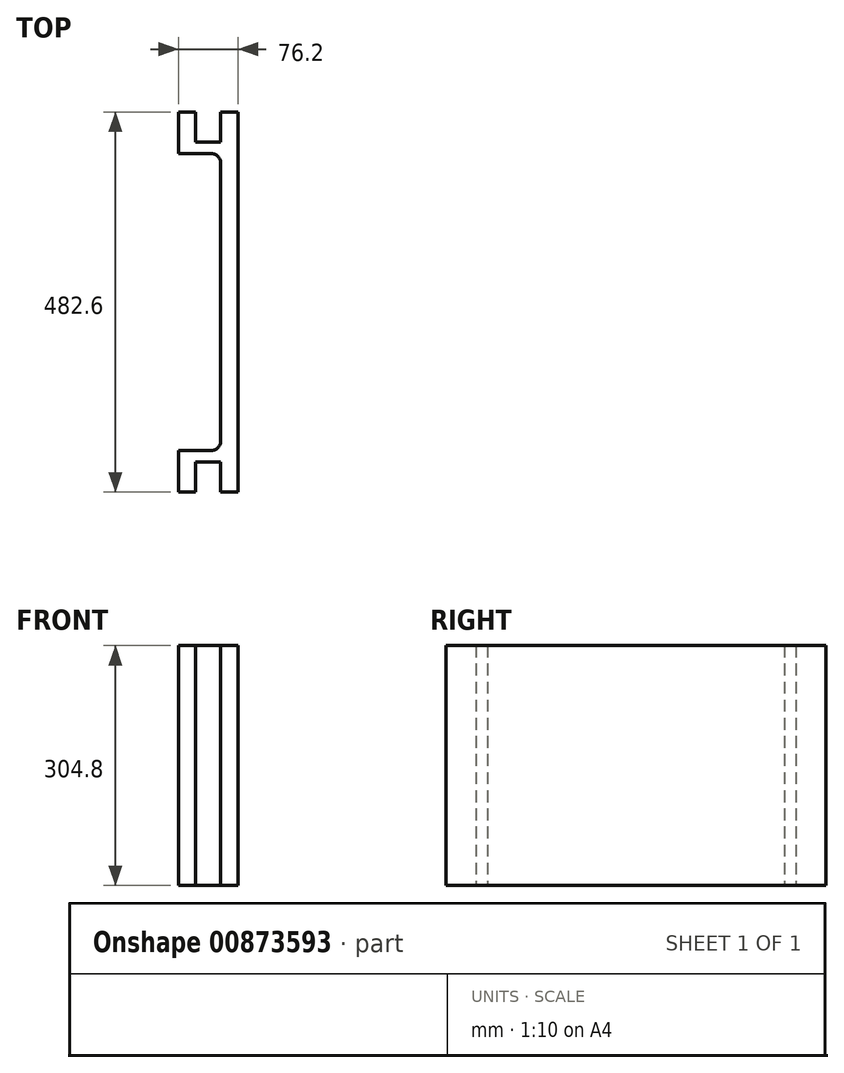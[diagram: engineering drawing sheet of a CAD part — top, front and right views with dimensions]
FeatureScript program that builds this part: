
annotation { "Feature Type Name" : "Feature", "Feature Type Description" : "" }
export const myFeature = defineFeature(function(context is Context, id is Id, definition is map)
    precondition{}
    {
        {
            var Q0;
            Q0=qCreatedBy(makeId("Top.planeOp"),FACE);
            var sketch = newSketch(context, id + "F0", { "sketchPlane" : qUnion([Q0])});
            skLineSegment(sketch, "E0.bottom", {"start": v(0, 0) * mm, "end": v(22.22, 0) * mm});
            skLineSegment(sketch, "E0.top", {"start": v(0, 482.6) * mm, "end": v(22.22, 482.6) * mm});
            skLineSegment(sketch, "E0.right", {"start": v(76.2, 0) * mm, "end": v(76.2, 482.6) * mm});
            skLineSegment(sketch, "E1", {"start": v(0, 241.3) * mm, "end": v(242.2, 241.3) * mm, "construction": true});
            skLineSegment(sketch, "E2", {"start": v(38.1, 482.6) * mm, "end": v(38.1, -58.83) * mm, "construction": true});
            skLineSegment(sketch, "E3", {"start": v(22.22, 482.6) * mm, "end": v(22.22, 444.5) * mm});
            skLineSegment(sketch, "E4", {"start": v(22.22, 444.5) * mm, "end": v(53.98, 444.5) * mm});
            skLineSegment(sketch, "E5", {"start": v(53.97, 444.5) * mm, "end": v(53.97, 482.6) * mm});
            skLineSegment(sketch, "E6.trimOffspring", {"start": v(53.98, 482.6) * mm, "end": v(76.2, 482.6) * mm});
            skLineSegment(sketch, "E7.MirrorCS", {"start": v(22.22, 0) * mm, "end": v(22.22, 38.1) * mm});
            skLineSegment(sketch, "E8.MirrorCS", {"start": v(22.22, 38.1) * mm, "end": v(53.97, 38.1) * mm});
            skLineSegment(sketch, "E9.MirrorCS", {"start": v(53.97, 38.1) * mm, "end": v(53.97, 0) * mm});
            skLineSegment(sketch, "E10.trimOffspring", {"start": v(53.97, 0) * mm, "end": v(76.2, 0) * mm});
            skLineSegment(sketch, "E11.bottom", {"start": v(53.97, 430.05) * mm, "end": v(22.22, 430.05) * mm});
            skLineSegment(sketch, "E11.top", {"start": v(53.98, 52.55) * mm, "end": v(22.22, 52.55) * mm});
            skLineSegment(sketch, "E11.left", {"start": v(53.97, 430.05) * mm, "end": v(53.97, 52.55) * mm});
            skLineSegment(sketch, "E11.right", {"start": v(22.22, 430.05) * mm, "end": v(22.22, 52.55) * mm, "construction": true});
            skPoint(sketch, "E11.middle", {"position": v(38.1, 241.3) * mm});
            skLineSegment(sketch, "E12", {"start": v(22.22, 430.05) * mm, "end": v(0, 430.05) * mm});
            skLineSegment(sketch, "E13", {"start": v(22.22, 52.55) * mm, "end": v(0, 52.55) * mm});
            skLineSegment(sketch, "E14", {"start": v(0, 482.6) * mm, "end": v(0, 430.05) * mm});
            skLineSegment(sketch, "E15", {"start": v(0, 52.55) * mm, "end": v(0, 0) * mm});
            skSolve(sketch);
        }
        {
            var Q0;
            Q0 = qSketchRegion(id + "F0", true);
            extrude(context, id + "F1", {"entities" : qUnion([Q0]), "depth" : 304.8 * mm, "offsetDistance" : 25.4 * mm});
        }
        {
            var Q0;
            Q0=makeQuery(id+"F1.opExtrude","SWEPT_EDGE",EDGE,{"disambiguationData":[OSD([sQuery(id+"F0.wireOp",EDGE,"E11.bottom"),sQuery(id+"F0.wireOp",EDGE,"E11.left")])]});
            var Q1;
            Q1=makeQuery(id+"F1.opExtrude","SWEPT_EDGE",EDGE,{"disambiguationData":[OSD([sQuery(id+"F0.wireOp",EDGE,"E11.top"),sQuery(id+"F0.wireOp",EDGE,"E11.left")])]});
            fillet(context, id + "F2", {"entities" : qUnion([Q0, Q1]), "radius" : 12.7 * mm, "tangentPropagation" : true, "allowEdgeOverflow" : false});
        }
    });
